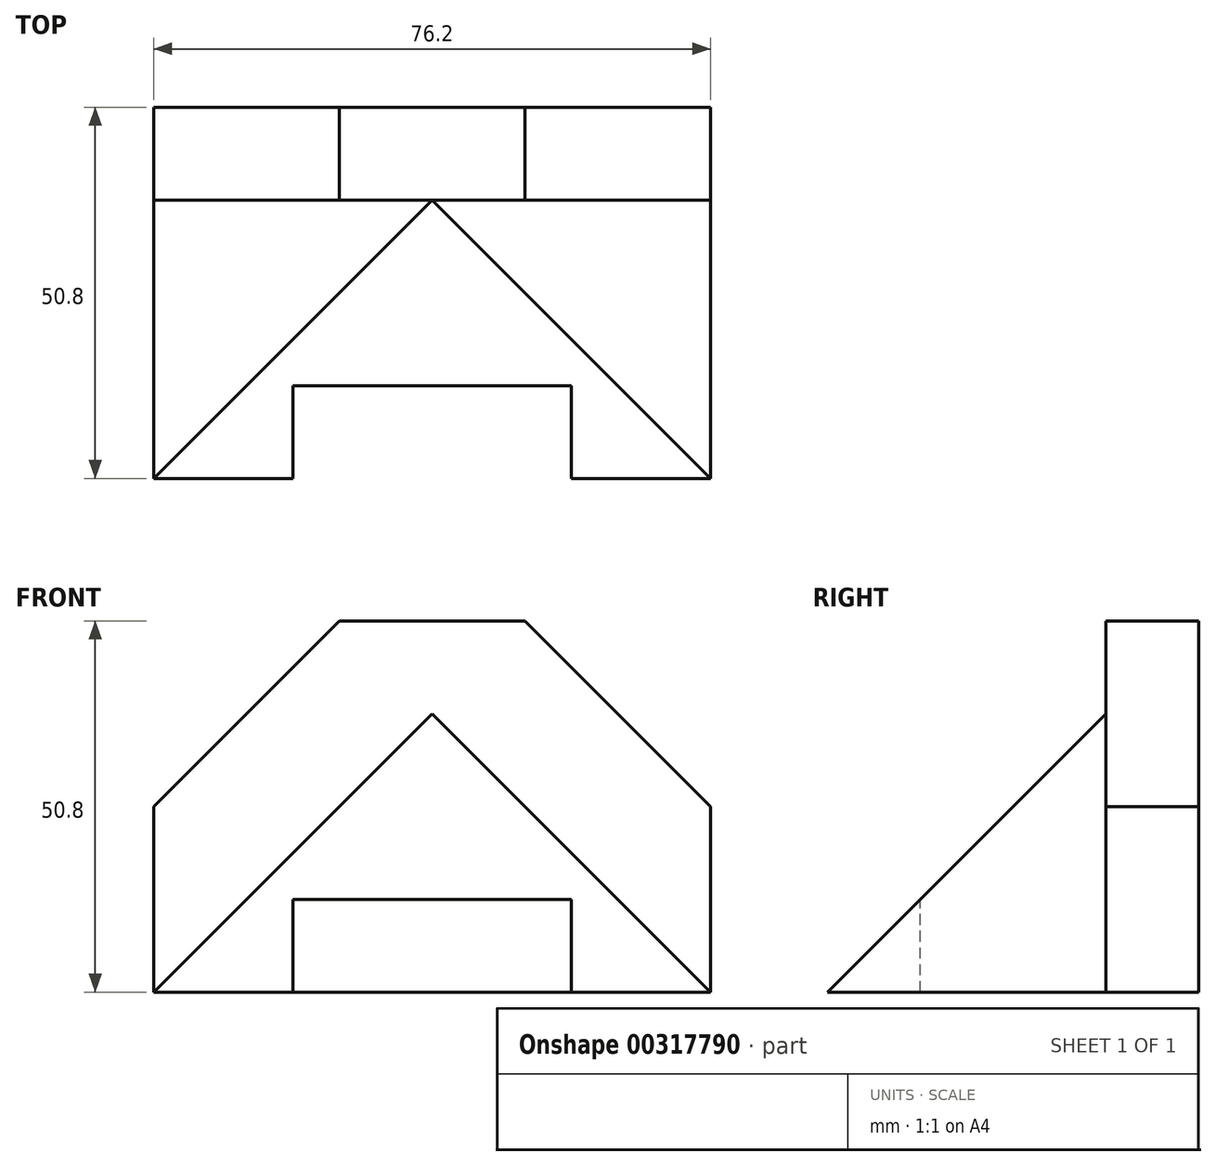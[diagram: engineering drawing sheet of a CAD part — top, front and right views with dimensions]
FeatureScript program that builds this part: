
annotation { "Feature Type Name" : "Feature", "Feature Type Description" : "" }
export const myFeature = defineFeature(function(context is Context, id is Id, definition is map)
    precondition{}
    {
        {
            var Q0;
            Q0=qCreatedBy(makeId("Front.planeOp"),FACE);
            var sketch = newSketch(context, id + "F0", { "sketchPlane" : qUnion([Q0])});
            skLineSegment(sketch, "E0", {"start": v(0, 25.4) * mm, "end": v(0, 0) * mm});
            skLineSegment(sketch, "E1", {"start": v(0, 0) * mm, "end": v(76.2, 0) * mm});
            skLineSegment(sketch, "E2", {"start": v(76.2, 0) * mm, "end": v(76.2, 25.4) * mm});
            skLineSegment(sketch, "E3", {"start": v(76.2, 25.4) * mm, "end": v(50.8, 50.8) * mm});
            skLineSegment(sketch, "E4", {"start": v(50.8, 50.8) * mm, "end": v(25.4, 50.8) * mm});
            skLineSegment(sketch, "E5", {"start": v(25.4, 50.8) * mm, "end": v(0, 25.4) * mm});
            skSolve(sketch);
        }
        {
            var Q0;
            Q0 = qSketchRegion(id + "F0", true);
            extrude(context, id + "F1", {"entities" : qUnion([Q0]), "oppositeDirection" : true, "depth" : 12.7 * mm});
        }
        {
            var Q0;
            Q0=makeQuery(id+"F1.opExtrude","CAP_FACE",FACE,{"disambiguationData":[OSD([sQuery(id+"F0.wireOp",EDGE,"E0"),sQuery(id+"F0.wireOp",EDGE,"E1"),sQuery(id+"F0.wireOp",EDGE,"E2"),sQuery(id+"F0.wireOp",EDGE,"E3"),sQuery(id+"F0.wireOp",EDGE,"E4"),sQuery(id+"F0.wireOp",EDGE,"E5")])],"isStart":true});
            var sketch = newSketch(context, id + "F2", { "sketchPlane" : qUnion([Q0])});
            skLineSegment(sketch, "E6", {"start": v(0, 0) * mm, "end": v(38.1, 38.1) * mm});
            skLineSegment(sketch, "E7", {"start": v(38.1, 38.1) * mm, "end": v(76.2, 0) * mm});
            skLineSegment(sketch, "E8", {"start": v(76.2, 0) * mm, "end": v(0, 0) * mm});
            skSolve(sketch);
        }
        {
            var Q0;
            Q0=makeQuery(id+"F2.imprint","IMPRINT",FACE,{"disambiguationData":[TD([[makeQuery(id+"F2.imprint","IMPRINT",EDGE,{"derivedFrom":sQuery(id+"F2.wireOp",EDGE,"E6")}),-1.0]])]});
            extrude(context, id + "F3", {"entities" : qUnion([Q0]), "operationType" : NewBodyOperationType.ADD, "depth" : 38.1 * mm});
        }
        {
            var Q0;
            Q0=makeQuery(id+"F1.opExtrude","SWEPT_FACE",FACE,{"disambiguationData":[OSD([sQuery(id+"F0.wireOp",EDGE,"E0")])]});
            var sketch = newSketch(context, id + "F4", { "sketchPlane" : qUnion([Q0])});
            skLineSegment(sketch, "E9", {"start": v(0, 38.1) * mm, "end": v(38.1, 0) * mm});
            skLineSegment(sketch, "E10", {"start": v(38.1, 0) * mm, "end": v(38.1, 38.1) * mm});
            skLineSegment(sketch, "E11", {"start": v(38.1, 38.1) * mm, "end": v(0, 38.1) * mm});
            skSolve(sketch);
        }
        {
            var Q0;
            Q0 = qSketchRegion(id + "F4", true);
            extrude(context, id + "F5", {"entities" : qUnion([Q0]), "operationType" : NewBodyOperationType.REMOVE, "endBound" : BoundingType.THROUGH_ALL, "oppositeDirection" : true, "depth" : 25.4 * mm});
        }
        {
            var Q0;
            Q0=makeQuery(id+"F1.opExtrude","SWEPT_FACE",FACE,{"disambiguationData":[OSD([sQuery(id+"F0.wireOp",EDGE,"E4")])]});
            var sketch = newSketch(context, id + "F6", { "sketchPlane" : qUnion([Q0])});
            skLineSegment(sketch, "E12", {"start": v(19.05, -38.1) * mm, "end": v(19.05, -25.4) * mm});
            skLineSegment(sketch, "E13", {"start": v(19.05, -25.4) * mm, "end": v(57.15, -25.4) * mm});
            skLineSegment(sketch, "E14", {"start": v(57.15, -25.4) * mm, "end": v(57.15, -38.1) * mm});
            skLineSegment(sketch, "E15", {"start": v(57.15, -38.1) * mm, "end": v(19.05, -38.1) * mm});
            skLineSegment(sketch, "E16", {"start": v(38.1, 26.55) * mm, "end": v(38.1, -76.4) * mm, "construction": true});
            skPoint(sketch, "E16.startSnap0", {"position": v(38.1, 12.7) * mm});
            skSolve(sketch);
        }
        {
            var Q0;
            Q0 = qSketchRegion(id + "F6", true);
            extrude(context, id + "F7", {"entities" : qUnion([Q0]), "operationType" : NewBodyOperationType.REMOVE, "endBound" : BoundingType.THROUGH_ALL, "oppositeDirection" : true, "depth" : 25.4 * mm});
        }
    });
